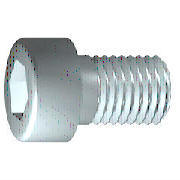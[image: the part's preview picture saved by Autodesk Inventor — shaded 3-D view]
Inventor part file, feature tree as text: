
AUTODESK INVENTOR PART (.ipt)
format: ipt  version: 2013 (Build 170138000, 138)  size: 189,952 bytes
history: native  units: mm (DEFAULTED — no unit token found)
features: sketch x2, extrude x1, plane x1, fillet x1
ambient origin geometry x7: Origin, YZ Plane, XY Plane, X Axis, Y Axis, Z Axis, Center Point
bodies: Solid1 (feature_tree), Body (feature_tree)
feature tree (5):
  extrude  "Slot"  Depth=0.306825mm
  plane  "Work Plane1"
  fillet  "Fillet2"  Radius=3.0mm
  sketch  "Sketch1"  dims[d1=4.693275mm d2=0.306825mm d3=3.0mm]
  sketch  "Sketch2"  dims[d4=1.5mm d5=60.0deg d6=3.0mm d7=3.0mm d8=2.886751mm d9=5.5mm d10=90.0deg d11=10.0mm d12=0.0mm d13=4.693275mm d14=0.0mm d15=0.306725mm d16=0.306725mm d17=0.3mm d19=0.0mm d26=6.0mm d27=45.0deg d28=0.0mm d29=0.0mm d30=0.1mm]
